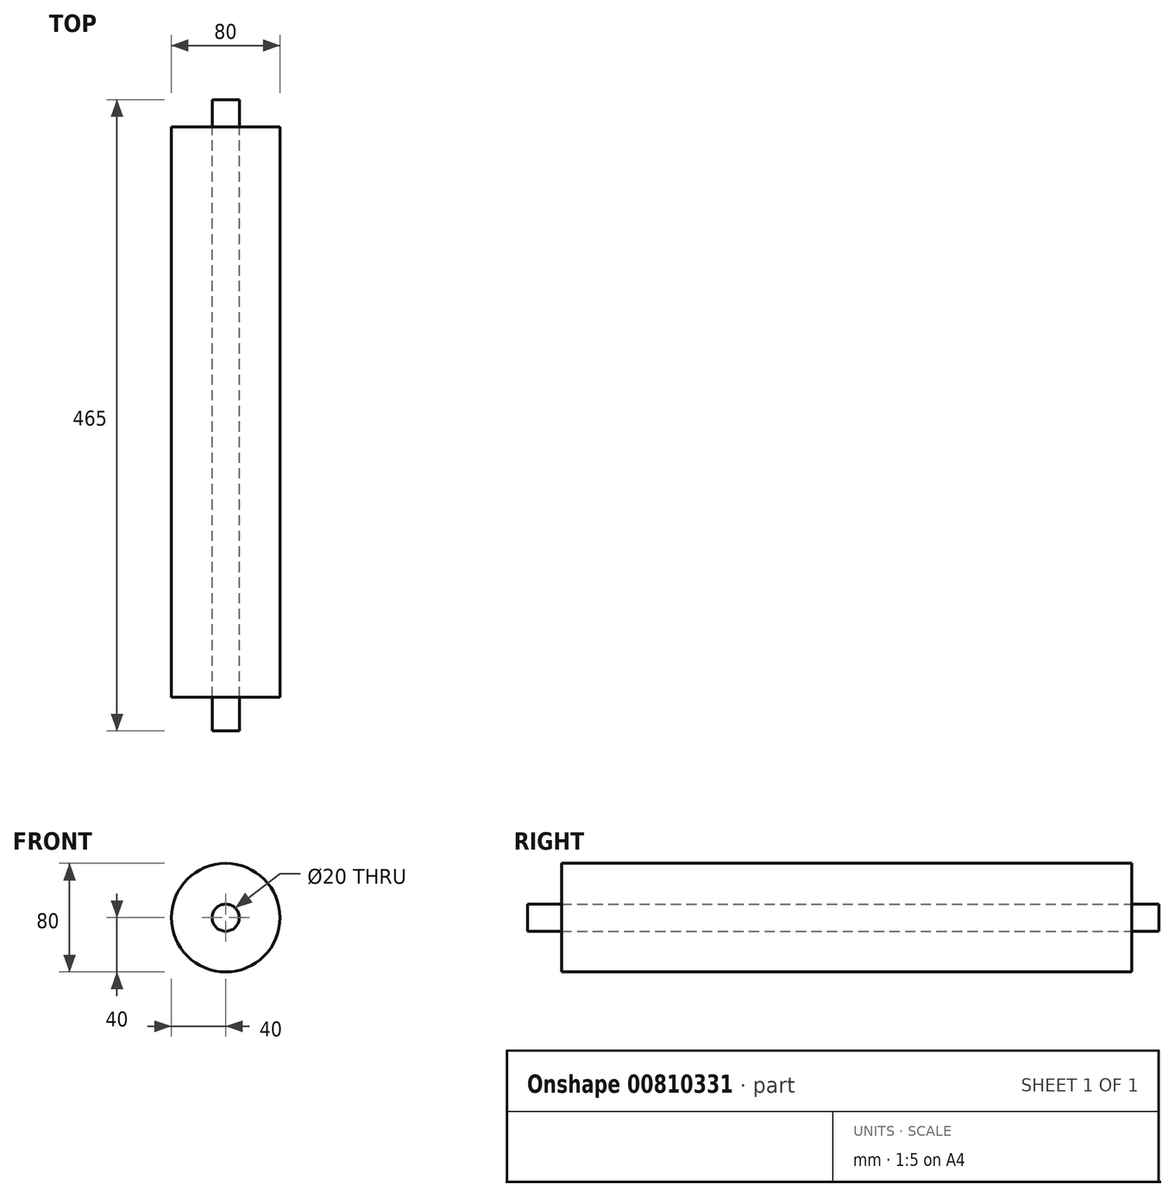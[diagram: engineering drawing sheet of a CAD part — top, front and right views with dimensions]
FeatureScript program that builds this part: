
annotation { "Feature Type Name" : "Feature", "Feature Type Description" : "" }
export const myFeature = defineFeature(function(context is Context, id is Id, definition is map)
    precondition{}
    {
        {
            var Q0;
            Q0=qCreatedBy(makeId("Front.planeOp"),FACE);
            var sketch = newSketch(context, id + "F0", { "sketchPlane" : qUnion([Q0])});
            skCircle(sketch, "E0", {"center": v(0, 0) * mm, "radius": 10 * mm});
            skSolve(sketch);
        }
        {
            var Q0;
            Q0 = qSketchRegion(id + "F0", true);
            extrude(context, id + "F1", {"entities" : qUnion([Q0]), "endBound" : BoundingType.SYMMETRIC, "depth" : 465 * mm, "offsetDistance" : 25.4 * mm});
        }
        {
            var Q0;
            Q0=makeQuery(id+"F1.opExtrude","CAP_FACE",FACE,{"disambiguationData":[OSD([sQuery(id+"F0.wireOp",EDGE,"E0")])],"isStart":false});
            cPlane(context, id + "F2", {"entities" : qUnion([Q0]), "cplaneType" : CPlaneType.OFFSET, "offset" : 235 * mm, "oppositeDirection" : true, "width" : 152.4 * mm, "height" : 152.4 * mm});
        }
        {
            var Q0;
            Q0=qCreatedBy(id+"F2.planeOp",FACE);
            var sketch = newSketch(context, id + "F3", { "sketchPlane" : qUnion([Q0])});
            skCircle(sketch, "E1", {"center": v(0, 0) * mm, "radius": 40 * mm});
            skCircle(sketch, "E2", {"center": v(0, 0) * mm, "radius": 10 * mm});
            skSolve(sketch);
        }
        {
            var Q0;
            Q0 = qSketchRegion(id + "F3", true);
            extrude(context, id + "F4", {"entities" : qUnion([Q0]), "endBound" : BoundingType.SYMMETRIC, "depth" : 420 * mm, "offsetDistance" : 25.4 * mm});
        }
    });
